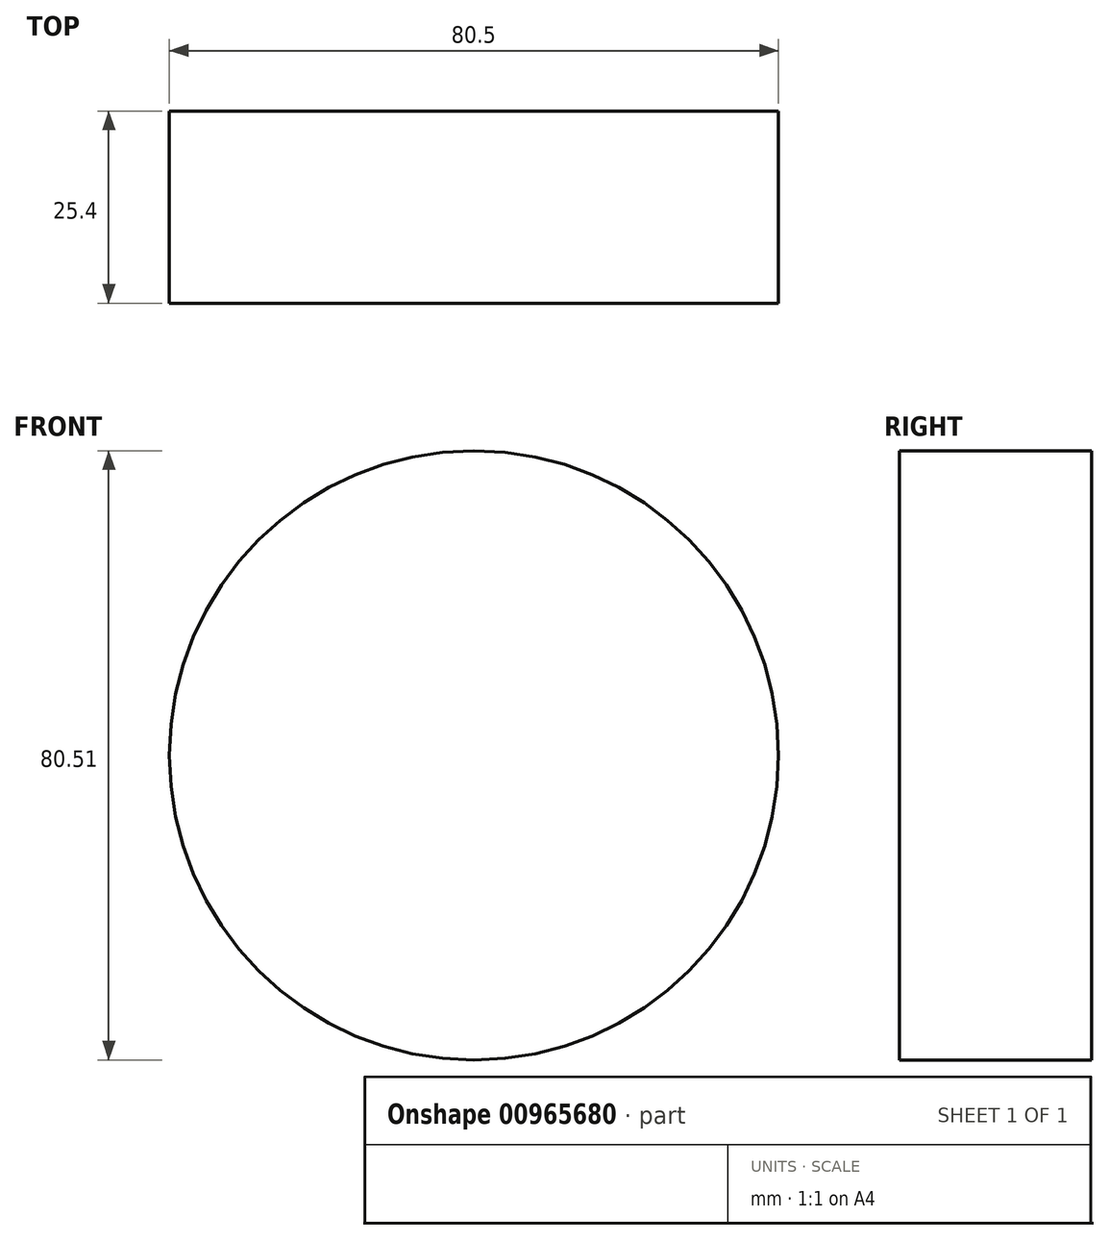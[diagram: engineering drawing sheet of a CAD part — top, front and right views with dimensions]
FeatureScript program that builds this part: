
annotation { "Feature Type Name" : "Feature", "Feature Type Description" : "" }
export const myFeature = defineFeature(function(context is Context, id is Id, definition is map)
    precondition{}
    {
        {
            var Q0;
            Q0=qCreatedBy(makeId("Front.planeOp"),FACE);
            var sketch = newSketch(context, id + "F0", { "sketchPlane" : qUnion([Q0])});
            skCircle(sketch, "E0", {"center": v(0, 40.25) * mm, "radius": 40.25 * mm});
            skSolve(sketch);
        }
        {
            var Q0;
            Q0 = qSketchRegion(id + "F0", true);
            extrude(context, id + "F1", {"entities" : qUnion([Q0]), "depth" : 25.4 * mm, "offsetDistance" : 25.4 * mm});
        }
    });
